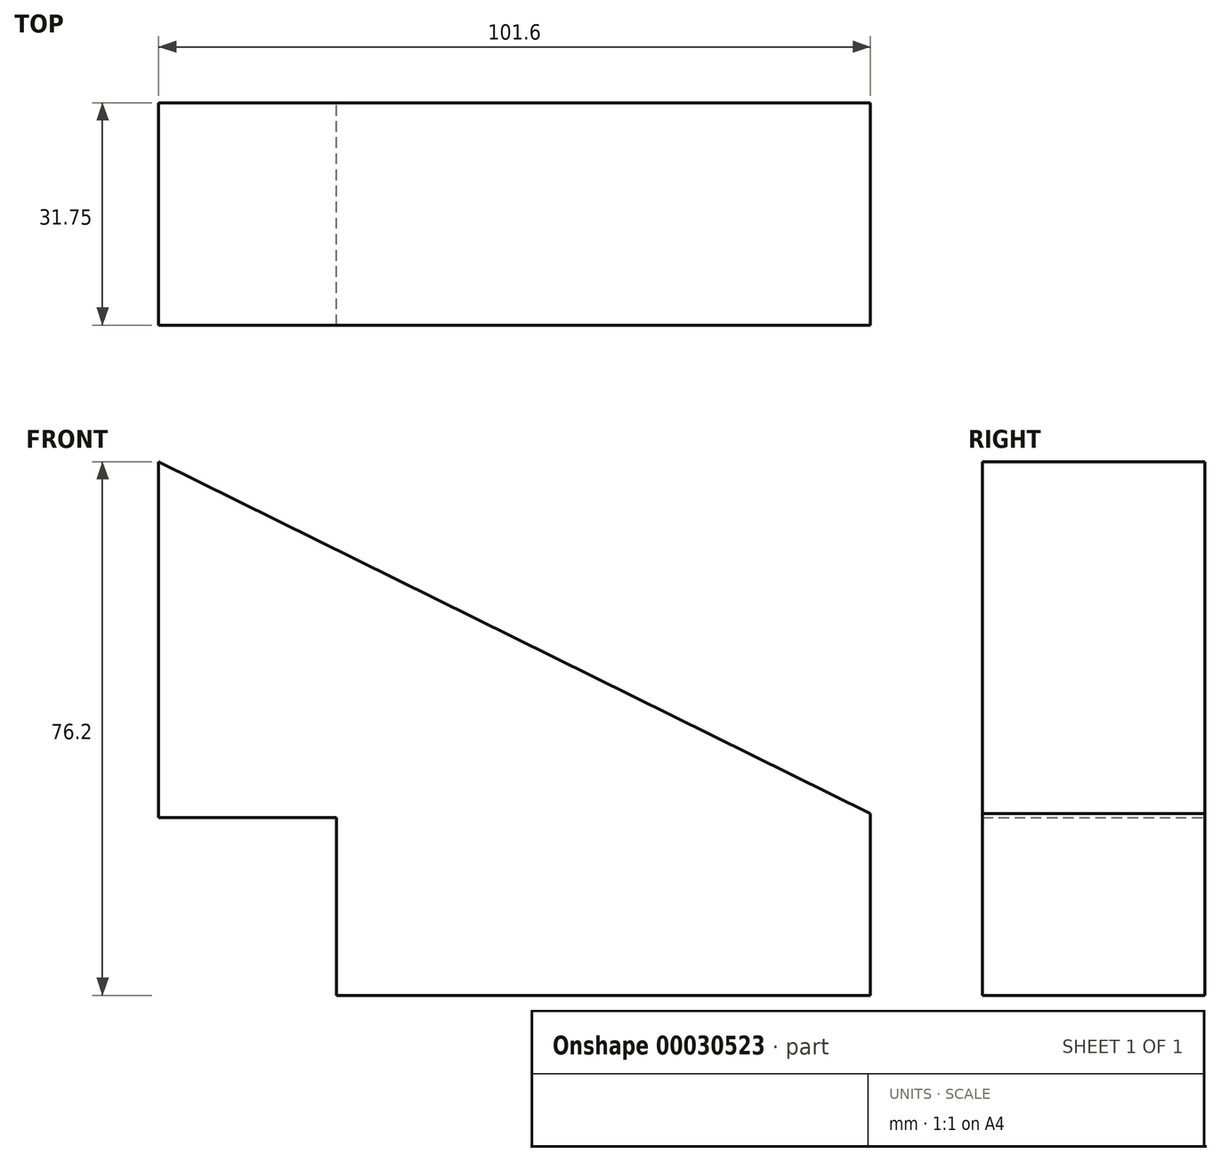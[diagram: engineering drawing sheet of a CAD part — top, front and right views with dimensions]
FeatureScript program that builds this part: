
annotation { "Feature Type Name" : "Feature", "Feature Type Description" : "" }
export const myFeature = defineFeature(function(context is Context, id is Id, definition is map)
    precondition{}
    {
        {
            var Q0;
            Q0=qCreatedBy(makeId("Front.planeOp"),FACE);
            var sketch = newSketch(context, id + "F0", { "sketchPlane" : qUnion([Q0])});
            skLineSegment(sketch, "E0", {"start": v(-56.97, -50.2) * mm, "end": v(19.23, -50.2) * mm});
            skLineSegment(sketch, "E1", {"start": v(19.23, -50.2) * mm, "end": v(19.23, -24.27) * mm});
            skLineSegment(sketch, "E2", {"start": v(-56.97, -50.2) * mm, "end": v(-56.97, -24.8) * mm});
            skLineSegment(sketch, "E3", {"start": v(-56.97, -24.8) * mm, "end": v(-82.37, -24.8) * mm});
            skLineSegment(sketch, "E4", {"start": v(-82.37, -24.8) * mm, "end": v(-82.37, 26) * mm});
            skLineSegment(sketch, "E5", {"start": v(-82.37, 26) * mm, "end": v(19.23, -24.27) * mm});
            skSolve(sketch);
        }
        {
            var Q0;
            Q0=makeQuery(id+"F0.imprint","IMPRINT",FACE,{"disambiguationData":[TD([[makeQuery(id+"F0.imprint","IMPRINT",EDGE,{"derivedFrom":sQuery(id+"F0.wireOp",EDGE,"E0")}),1.0]])]});
            extrude(context, id + "F1", {"entities" : qUnion([Q0]), "depth" : 31.75 * mm});
        }
    });
